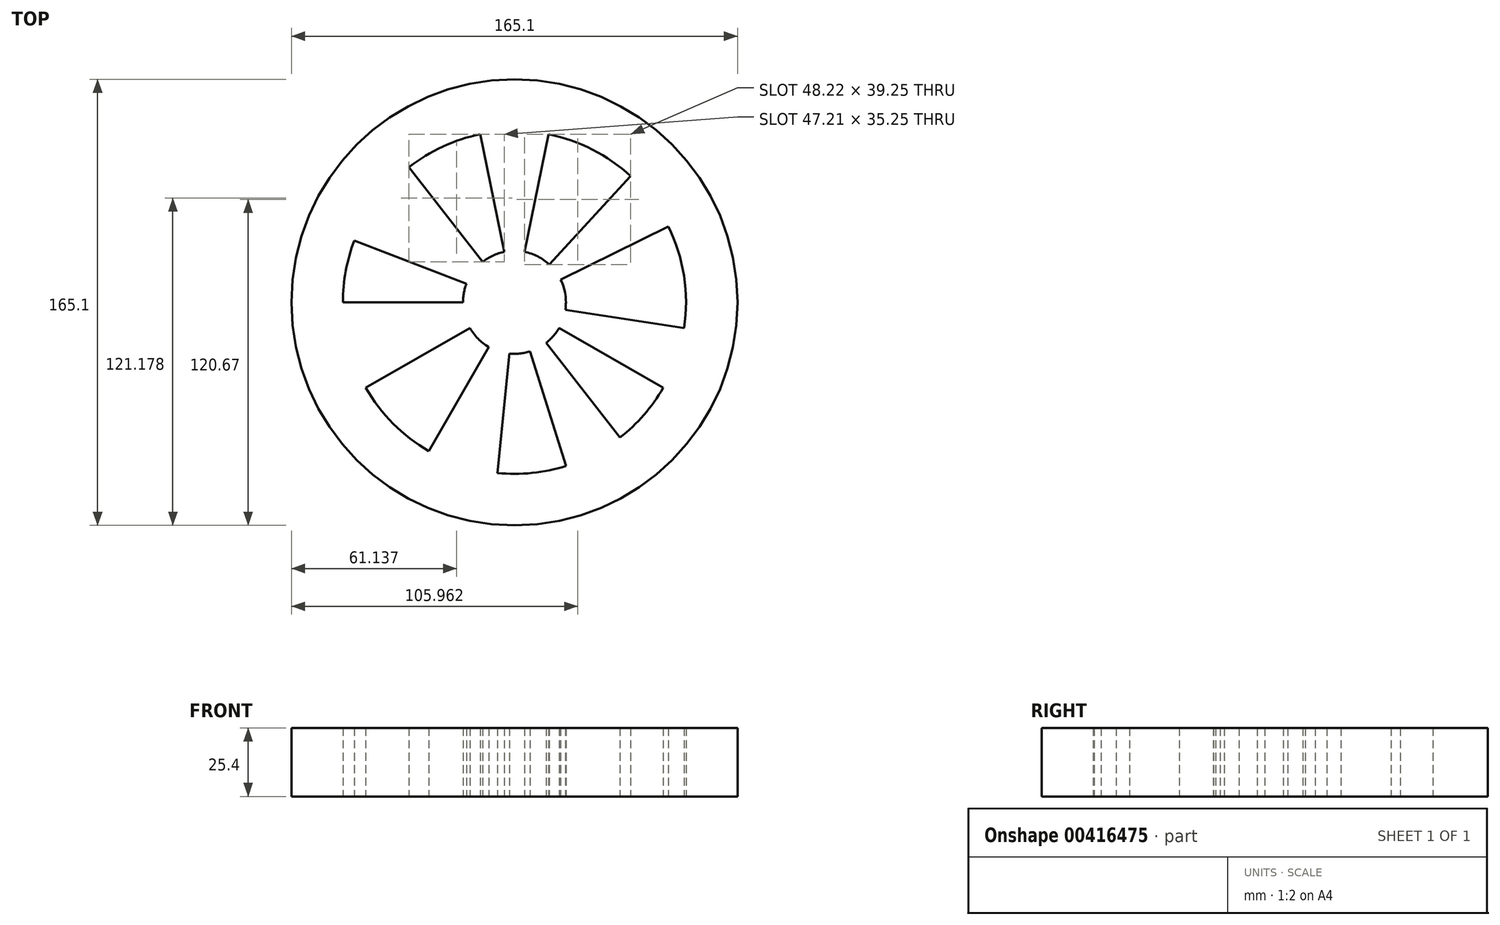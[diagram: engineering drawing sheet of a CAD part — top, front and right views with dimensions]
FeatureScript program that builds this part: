
annotation { "Feature Type Name" : "Feature", "Feature Type Description" : "" }
export const myFeature = defineFeature(function(context is Context, id is Id, definition is map)
    precondition{}
    {
        {
            var Q0;
            Q0=qCreatedBy(makeId("Top.planeOp"),FACE);
            var sketch = newSketch(context, id + "F0", { "sketchPlane" : qUnion([Q0])});
            skCircle(sketch, "E0", {"center": v(0, 0) * mm, "radius": 82.55 * mm});
            skCircle(sketch, "E1", {"center": v(0, 0) * mm, "radius": 63.5 * mm});
            skCircle(sketch, "E2", {"center": v(0, 0) * mm, "radius": 19.05 * mm});
            skLineSegment(sketch, "E3", {"start": v(-12.62, 62.23) * mm, "end": v(-3.79, 18.67) * mm});
            skLineSegment(sketch, "E4", {"start": v(12.62, 62.23) * mm, "end": v(3.79, 18.67) * mm});
            skLineSegment(sketch, "E5", {"start": v(12.91, 14) * mm, "end": v(43.04, 46.7) * mm});
            skLineSegment(sketch, "E6", {"start": v(17.08, 8.44) * mm, "end": v(56.93, 28.13) * mm});
            skLineSegment(sketch, "E7", {"start": v(18.84, -2.85) * mm, "end": v(62.79, -9.5) * mm});
            skLineSegment(sketch, "E8", {"start": v(16.52, -9.5) * mm, "end": v(55.05, -31.64) * mm});
            skLineSegment(sketch, "E9", {"start": v(11.71, -15.02) * mm, "end": v(39.04, -50.08) * mm});
            skLineSegment(sketch, "E10", {"start": v(5.73, -18.17) * mm, "end": v(19.1, -60.56) * mm});
            skLineSegment(sketch, "E11", {"start": v(-1.88, -18.96) * mm, "end": v(-6.27, -63.19) * mm});
            skLineSegment(sketch, "E12", {"start": v(-9.5, -16.52) * mm, "end": v(-31.64, -55.05) * mm});
            skLineSegment(sketch, "E13", {"start": v(-16.52, -9.5) * mm, "end": v(-55.05, -31.64) * mm});
            skLineSegment(sketch, "E14", {"start": v(-19.05, 0) * mm, "end": v(-63.5, 0) * mm});
            skLineSegment(sketch, "E15", {"start": v(-17.77, 6.87) * mm, "end": v(-59.22, 22.92) * mm});
            skLineSegment(sketch, "E16", {"start": v(-11.71, 15.02) * mm, "end": v(-39.04, 50.08) * mm});
            skSolve(sketch);
        }
        {
            var Q0;
            Q0=makeQuery(id+"F0.imprint","IMPRINT",FACE,{"disambiguationData":[TD([[makeQuery(id+"F0.imprint","IMPRINT",EDGE,{"derivedFrom":sQuery(id+"F0.wireOp",EDGE,"E0")}),1.0]])]});
            extrude(context, id + "F1", {"entities" : qUnion([Q0]), "depth" : 25.4 * mm});
        }
        {
            var Q0;
            {var subQ0=sQuery(id+"F0.wireOp",EDGE,"E15");Q0=makeQuery(id+"F0.imprint","IMPRINT",FACE,{"disambiguationData":[TD([[makeQuery(id+"F0.imprint","IMPRINT",EDGE,{"derivedFrom":subQ0}),-1.0]])]});}
            var Q1;
            {var subQ0=sQuery(id+"F0.wireOp",EDGE,"E13");Q1=makeQuery(id+"F0.imprint","IMPRINT",FACE,{"disambiguationData":[TD([[makeQuery(id+"F0.imprint","IMPRINT",EDGE,{"derivedFrom":subQ0}),-1.0]])]});}
            var Q2;
            {var subQ0=sQuery(id+"F0.wireOp",EDGE,"E11");Q2=makeQuery(id+"F0.imprint","IMPRINT",FACE,{"disambiguationData":[TD([[makeQuery(id+"F0.imprint","IMPRINT",EDGE,{"derivedFrom":subQ0}),-1.0]])]});}
            var Q3;
            {var subQ0=sQuery(id+"F0.wireOp",EDGE,"E9");Q3=makeQuery(id+"F0.imprint","IMPRINT",FACE,{"disambiguationData":[TD([[makeQuery(id+"F0.imprint","IMPRINT",EDGE,{"derivedFrom":subQ0}),-1.0]])]});}
            var Q4;
            {var subQ0=sQuery(id+"F0.wireOp",EDGE,"E7");Q4=makeQuery(id+"F0.imprint","IMPRINT",FACE,{"disambiguationData":[TD([[makeQuery(id+"F0.imprint","IMPRINT",EDGE,{"derivedFrom":subQ0}),-1.0]])]});}
            var Q5;
            {var subQ0=sQuery(id+"F0.wireOp",EDGE,"E5");Q5=makeQuery(id+"F0.imprint","IMPRINT",FACE,{"disambiguationData":[TD([[makeQuery(id+"F0.imprint","IMPRINT",EDGE,{"derivedFrom":subQ0}),-1.0]])]});}
            var Q6;
            {var subQ0=sQuery(id+"F0.wireOp",EDGE,"E3");Q6=makeQuery(id+"F0.imprint","IMPRINT",FACE,{"disambiguationData":[TD([[makeQuery(id+"F0.imprint","IMPRINT",EDGE,{"derivedFrom":subQ0}),1.0]])]});}
            var Q7;
            {var subQ0=sQuery(id+"F0.wireOp",EDGE,"E2");var subQ8=makeQuery(id+"F0.imprint","INTERSECT",VERTEX,{"derivedFrom":[subQ0,sQuery(id+"F0.wireOp",EDGE,"E5")]});Q7=makeQuery(id+"F0.imprint","IMPRINT",FACE,{"disambiguationData":[TD([[makeQuery(id+"F0.imprint","IMPRINT",EDGE,{"disambiguationData":[TD([[subQ8,1.0]])],"derivedFrom":subQ0}),1.0]])]});}
            extrude(context, id + "F2", {"entities" : qUnion([Q0, Q1, Q2, Q3, Q4, Q5, Q6, Q7]), "operationType" : NewBodyOperationType.ADD, "depth" : 25.4 * mm});
        }
    });
